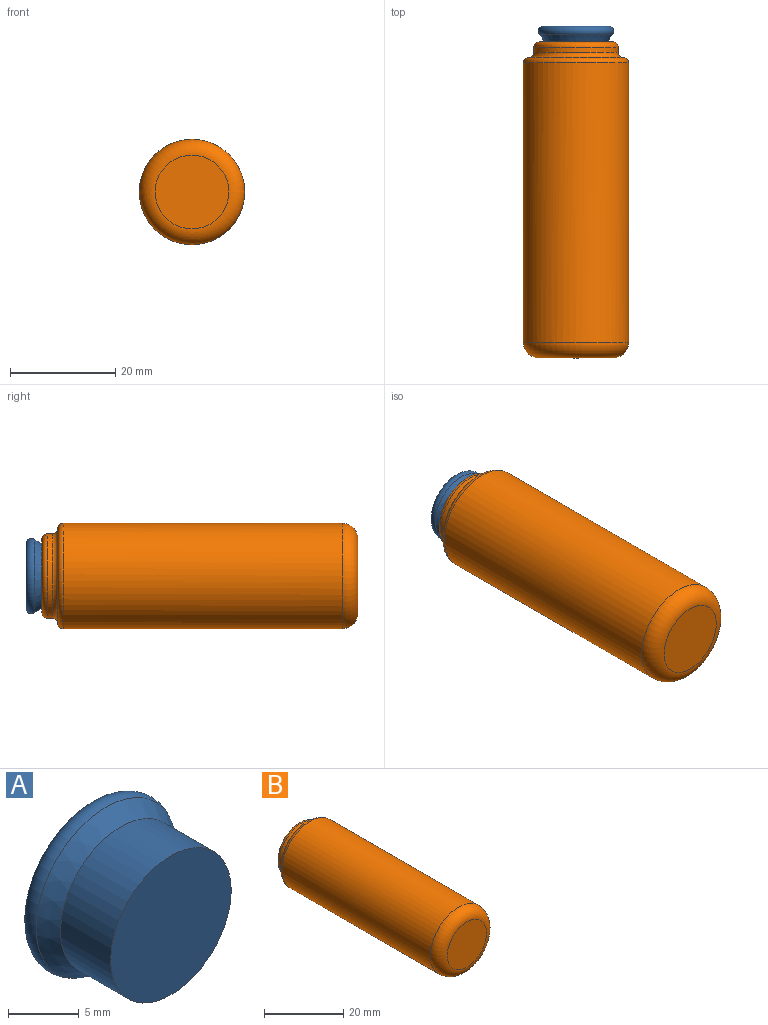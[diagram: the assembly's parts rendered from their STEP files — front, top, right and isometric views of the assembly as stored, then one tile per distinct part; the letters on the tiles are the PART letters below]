
ASSEMBLY  parts=2 mates=1
PART A: 5 faces, bbox 15.4x8x15.4 mm
  f0: cylinder r=6mm len=12mm, axis (0,-1,0), area 188.5mm2, adj f1,f3
  f1: plane 12x12mm, normal (0,-1,0), area 113.1mm2, adj f0
  f2: plane 12.27x12.27mm, normal (0,1,0), area 118.3mm2, adj f4
  f3: cone r=8mm half-angle=33.6deg, axis (0,1,0), area 71.5mm2, adj f0,f4
  f4: torus R=6.14mm, axis (0,-1,0), area 92.9mm2, adj f2,f3
PART B: 14 faces, bbox 21.6x60x21.6 mm
  f0: cylinder r=8mm len=49mm, axis (0,-1,0), area 2463mm2, adj f11,f12
  f1: cylinder r=6mm len=12mm, axis (0,-1,0), area 133.3mm2, adj f2,f13
  f2: plane 14x14mm, normal (0,1,0), area 40.8mm2, adj f1,f7
  f3: cylinder r=8mm len=16mm, axis (0,-1,0), area 50.3mm2, adj f7,f9
  f4: cylinder r=10mm len=53mm, axis (0,-1,0), area 3330.1mm2, adj f8,f10
  f5: plane 14x14mm, normal (0,-1,0), area 153.9mm2, adj f10
  f6: plane 12x12mm, normal (0,1,0), area 113.1mm2, adj f12
  f7: torus R=7mm, axis (0,1,0), area 75.4mm2, adj f2,f3
  f8: torus R=9mm, axis (0,-1,0), area 95.1mm2, adj f4,f9
  f9: torus R=9mm, axis (0,-1,0), area 82.5mm2, adj f3,f8
  f10: torus R=7mm, axis (0,1,0), area 263.8mm2, adj f4,f5
  f11: torus R=6mm, axis (0,1,0), area 100.7mm2, adj f0,f13
  f12: torus R=6mm, axis (0,-1,0), area 143.6mm2, adj f0,f6
  f13: torus R=8mm, axis (0,1,0), area 83.5mm2, adj f1,f11
PLACE A t=(-7.91,-19.54,2.3)mm
PLACE B t=(-7.91,-19.54,2.3)mm
MATE fastened B.f0 <-> A.f0  axis (0,1,0) through (-7.91,25.46,2.3)mm
